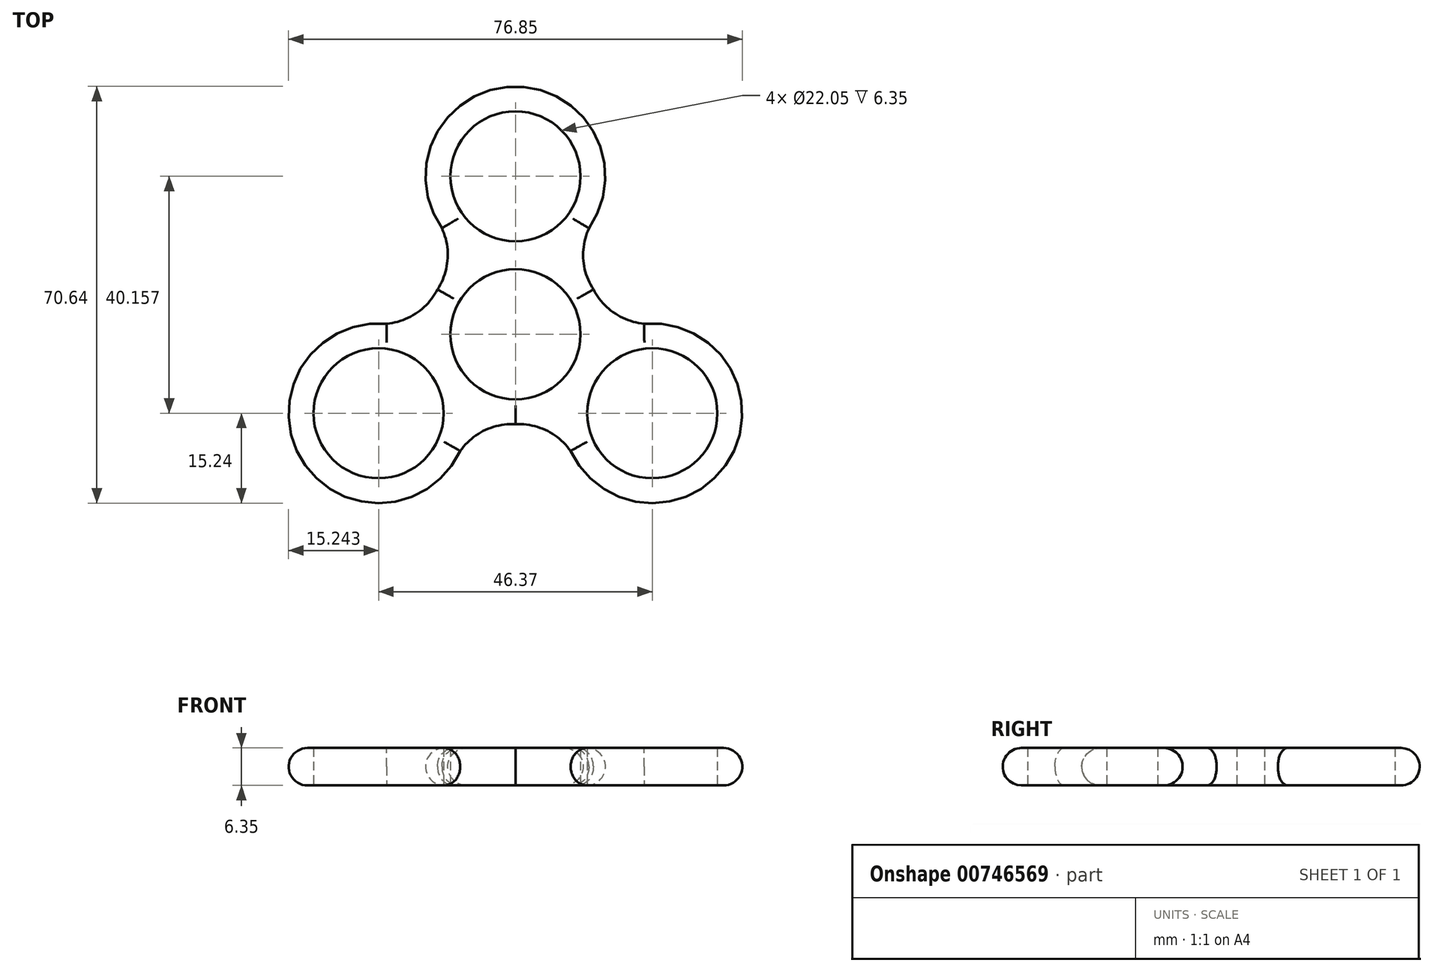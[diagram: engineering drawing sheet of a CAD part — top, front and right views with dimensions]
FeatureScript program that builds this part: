
annotation { "Feature Type Name" : "Feature", "Feature Type Description" : "" }
export const myFeature = defineFeature(function(context is Context, id is Id, definition is map)
    precondition{}
    {
        {
            var Q0;
            Q0=qCreatedBy(makeId("Top.planeOp"),FACE);
            var sketch = newSketch(context, id + "F0", { "sketchPlane" : qUnion([Q0])});
            skCircle(sketch, "E0", {"center": v(-0.7, 0.42) * mm, "radius": 11.02 * mm});
            skCircle(sketch, "E1", {"center": v(-0.7, 0.42) * mm, "radius": 15.24 * mm});
            skCircle(sketch, "E2", {"center": v(-0.7, 27.19) * mm, "radius": 11.02 * mm});
            skCircle(sketch, "E3", {"center": v(-0.7, 27.19) * mm, "radius": 15.24 * mm});
            skCircle(sketch, "E4.1.0", {"center": v(-23.88, -12.97) * mm, "radius": 15.24 * mm});
            skCircle(sketch, "E4.1.1", {"center": v(-23.88, -12.97) * mm, "radius": 11.02 * mm});
            skCircle(sketch, "E4.2.0", {"center": v(22.5, -12.97) * mm, "radius": 15.24 * mm});
            skCircle(sketch, "E4.2.1", {"center": v(22.5, -12.97) * mm, "radius": 11.02 * mm});
            skArc(sketch, "E5", {"start": v(-0.7, -14.82) * mm, "mid": v(-5.95, -15.9) * mm, "end": v(-10.04, -19.37) * mm});
            skArc(sketch, "E6.MirrorCS", {"start": v(-0.7, -14.82) * mm, "mid": v(4.57, -15.9) * mm, "end": v(8.66, -19.37) * mm});
            skArc(sketch, "E7.1.0", {"start": v(12.5, 8.04) * mm, "mid": v(10.8, 13.13) * mm, "end": v(11.76, 18.4) * mm});
            skArc(sketch, "E7.1.1", {"start": v(12.5, 8.04) * mm, "mid": v(16.06, 4.01) * mm, "end": v(21.12, 2.2) * mm});
            skArc(sketch, "E7.2.0", {"start": v(-13.9, 8.04) * mm, "mid": v(-17.44, 4.01) * mm, "end": v(-22.5, 2.2) * mm});
            skArc(sketch, "E7.2.1", {"start": v(-13.9, 8.04) * mm, "mid": v(-12.18, 13.13) * mm, "end": v(-13.15, 18.4) * mm});
            skLineSegment(sketch, "E7.anchor1", {"start": v(-0.7, 0.42) * mm, "end": v(-0.13, -25.57) * mm, "construction": true});
            skLineSegment(sketch, "E7.anchor2", {"start": v(-0.7, 0.42) * mm, "end": v(-23.48, 12.92) * mm, "construction": true});
            skSolve(sketch);
        }
        {
            var Q0;
            Q0=makeQuery(id+"F0.imprint","IMPRINT",FACE,{"disambiguationData":[TD([[makeQuery(id+"F0.imprint","IMPRINT",EDGE,{"derivedFrom":sQuery(id+"F0.wireOp",EDGE,"E2")}),-1.0]])]});
            var Q1;
            {var subQ0=sQuery(id+"F0.wireOp",EDGE,"E7.2.1");var subQ1=sQuery(id+"F0.wireOp",EDGE,"E1");var subQ2=makeQuery(id+"F0.imprint","INTERSECT",VERTEX,{"derivedFrom":[subQ1,subQ0]});Q1=makeQuery(id+"F0.imprint","IMPRINT",FACE,{"disambiguationData":[TD([[makeQuery(id+"F0.imprint","IMPRINT",EDGE,{"disambiguationData":[TD([[subQ2,1.0]])],"derivedFrom":subQ1}),-1.0]])]});}
            var Q2;
            {var subQ0=sQuery(id+"F0.wireOp",EDGE,"E7.2.0");var subQ1=sQuery(id+"F0.wireOp",EDGE,"E1");var subQ2=makeQuery(id+"F0.imprint","INTERSECT",VERTEX,{"derivedFrom":[subQ1,subQ0]});Q2=makeQuery(id+"F0.imprint","IMPRINT",FACE,{"disambiguationData":[TD([[makeQuery(id+"F0.imprint","IMPRINT",EDGE,{"disambiguationData":[TD([[subQ2,-1.0]])],"derivedFrom":subQ1}),-1.0]])]});}
            var Q3;
            {var subQ0=sQuery(id+"F0.wireOp",EDGE,"E7.1.0");var subQ1=sQuery(id+"F0.wireOp",EDGE,"E1");var subQ2=makeQuery(id+"F0.imprint","INTERSECT",VERTEX,{"derivedFrom":[subQ1,subQ0]});Q3=makeQuery(id+"F0.imprint","IMPRINT",FACE,{"disambiguationData":[TD([[makeQuery(id+"F0.imprint","IMPRINT",EDGE,{"disambiguationData":[TD([[subQ2,-1.0]])],"derivedFrom":subQ1}),-1.0]])]});}
            var Q4;
            {var subQ0=sQuery(id+"F0.wireOp",EDGE,"E7.1.1");var subQ1=sQuery(id+"F0.wireOp",EDGE,"E1");var subQ2=makeQuery(id+"F0.imprint","INTERSECT",VERTEX,{"derivedFrom":[subQ1,subQ0]});Q4=makeQuery(id+"F0.imprint","IMPRINT",FACE,{"disambiguationData":[TD([[makeQuery(id+"F0.imprint","IMPRINT",EDGE,{"disambiguationData":[TD([[subQ2,1.0]])],"derivedFrom":subQ1}),-1.0]])]});}
            var Q5;
            Q5=makeQuery(id+"F0.imprint","IMPRINT",FACE,{"disambiguationData":[TD([[makeQuery(id+"F0.imprint","IMPRINT",EDGE,{"derivedFrom":sQuery(id+"F0.wireOp",EDGE,"E0")}),-1.0]])]});
            var Q6;
            {var subQ0=sQuery(id+"F0.wireOp",EDGE,"E4.2.0");var subQ1=sQuery(id+"F0.wireOp",EDGE,"E1");var subQ2=makeQuery(id+"F0.imprint","INTERSECT",VERTEX,{"disambiguationData":[OD(0.0)],"derivedFrom":[subQ1,subQ0]});Q6=makeQuery(id+"F0.imprint","IMPRINT",FACE,{"disambiguationData":[TD([[makeQuery(id+"F0.imprint","IMPRINT",EDGE,{"disambiguationData":[TD([[subQ2,-1.0]])],"derivedFrom":subQ1}),1.0]])]});}
            var Q7;
            {var subQ0=sQuery(id+"F0.wireOp",EDGE,"E3");var subQ1=sQuery(id+"F0.wireOp",EDGE,"E1");var subQ2=makeQuery(id+"F0.imprint","INTERSECT",VERTEX,{"disambiguationData":[OD(0.0)],"derivedFrom":[subQ1,subQ0]});Q7=makeQuery(id+"F0.imprint","IMPRINT",FACE,{"disambiguationData":[TD([[makeQuery(id+"F0.imprint","IMPRINT",EDGE,{"disambiguationData":[TD([[subQ2,-1.0]])],"derivedFrom":subQ1}),1.0]])]});}
            var Q8;
            {var subQ0=sQuery(id+"F0.wireOp",EDGE,"E4.1.0");var subQ1=sQuery(id+"F0.wireOp",EDGE,"E1");var subQ2=makeQuery(id+"F0.imprint","INTERSECT",VERTEX,{"disambiguationData":[OD(0.0)],"derivedFrom":[subQ1,subQ0]});Q8=makeQuery(id+"F0.imprint","IMPRINT",FACE,{"disambiguationData":[TD([[makeQuery(id+"F0.imprint","IMPRINT",EDGE,{"disambiguationData":[TD([[subQ2,-1.0]])],"derivedFrom":subQ1}),1.0]])]});}
            var Q9;
            Q9=makeQuery(id+"F0.imprint","IMPRINT",FACE,{"disambiguationData":[TD([[makeQuery(id+"F0.imprint","IMPRINT",EDGE,{"derivedFrom":sQuery(id+"F0.wireOp",EDGE,"E4.1.1")}),-1.0]])]});
            var Q10;
            {var subQ0=sQuery(id+"F0.wireOp",EDGE,"E5");var subQ1=sQuery(id+"F0.wireOp",EDGE,"E1");var subQ2=makeQuery(id+"F0.imprint","INTERSECT",VERTEX,{"derivedFrom":[subQ1,subQ0]});Q10=makeQuery(id+"F0.imprint","IMPRINT",FACE,{"disambiguationData":[TD([[makeQuery(id+"F0.imprint","IMPRINT",EDGE,{"disambiguationData":[TD([[subQ2,1.0]])],"derivedFrom":subQ1}),-1.0]])]});}
            var Q11;
            {var subQ0=sQuery(id+"F0.wireOp",EDGE,"E6.MirrorCS");var subQ1=sQuery(id+"F0.wireOp",EDGE,"E1");var subQ2=makeQuery(id+"F0.imprint","INTERSECT",VERTEX,{"derivedFrom":[subQ1,subQ0]});Q11=makeQuery(id+"F0.imprint","IMPRINT",FACE,{"disambiguationData":[TD([[makeQuery(id+"F0.imprint","IMPRINT",EDGE,{"disambiguationData":[TD([[subQ2,-1.0]])],"derivedFrom":subQ1}),-1.0]])]});}
            var Q12;
            Q12=makeQuery(id+"F0.imprint","IMPRINT",FACE,{"disambiguationData":[TD([[makeQuery(id+"F0.imprint","IMPRINT",EDGE,{"derivedFrom":sQuery(id+"F0.wireOp",EDGE,"E4.2.1")}),-1.0]])]});
            extrude(context, id + "F1", {"entities" : qUnion([Q0, Q1, Q2, Q3, Q4, Q5, Q6, Q7, Q8, Q9, Q10, Q11, Q12]), "depth" : 6.35 * mm, "offsetDistance" : 25.4 * mm});
        }
        {
            var Q0;
            Q0=makeQuery(id+"F1.opExtrude","CAP_EDGE",EDGE,{"disambiguationData":[OSD([sQuery(id+"F0.wireOp",EDGE,"E3")])],"isStart":false});
            var Q1;
            Q1=makeQuery(id+"F1.opExtrude","CAP_EDGE",EDGE,{"disambiguationData":[OSD([sQuery(id+"F0.wireOp",EDGE,"E7.2.1")])],"isStart":false});
            var Q2;
            Q2=makeQuery(id+"F1.opExtrude","CAP_EDGE",EDGE,{"disambiguationData":[OSD([sQuery(id+"F0.wireOp",EDGE,"E7.2.0")])],"isStart":false});
            var Q3;
            Q3=makeQuery(id+"F1.opExtrude","CAP_EDGE",EDGE,{"disambiguationData":[OSD([sQuery(id+"F0.wireOp",EDGE,"E4.1.0")])],"isStart":false});
            var Q4;
            Q4=makeQuery(id+"F1.opExtrude","CAP_EDGE",EDGE,{"disambiguationData":[OSD([sQuery(id+"F0.wireOp",EDGE,"E5")])],"isStart":false});
            var Q5;
            Q5=makeQuery(id+"F1.opExtrude","CAP_EDGE",EDGE,{"disambiguationData":[OSD([sQuery(id+"F0.wireOp",EDGE,"E7.1.0")])],"isStart":false});
            var Q6;
            Q6=makeQuery(id+"F1.opExtrude","CAP_EDGE",EDGE,{"disambiguationData":[OSD([sQuery(id+"F0.wireOp",EDGE,"E4.2.0")])],"isStart":false});
            var Q7;
            Q7=makeQuery(id+"F1.opExtrude","CAP_EDGE",EDGE,{"disambiguationData":[OSD([sQuery(id+"F0.wireOp",EDGE,"E7.1.1")])],"isStart":false});
            var Q8;
            Q8=makeQuery(id+"F1.opExtrude","CAP_EDGE",EDGE,{"disambiguationData":[OSD([sQuery(id+"F0.wireOp",EDGE,"E6.MirrorCS")])],"isStart":false});
            fillet(context, id + "F2", {"entities" : qUnion([Q0, Q1, Q2, Q3, Q4, Q5, Q6, Q7, Q8]), "radius" : 3.17 * mm, "tangentPropagation" : true, "allowEdgeOverflow" : false});
        }
        {
            var Q0;
            Q0=makeQuery(id+"F1.opExtrude","CAP_EDGE",EDGE,{"disambiguationData":[OSD([sQuery(id+"F0.wireOp",EDGE,"E4.1.0")])],"isStart":true});
            var Q1;
            Q1=makeQuery(id+"F1.opExtrude","CAP_EDGE",EDGE,{"disambiguationData":[OSD([sQuery(id+"F0.wireOp",EDGE,"E5")])],"isStart":true});
            var Q2;
            Q2=makeQuery(id+"F1.opExtrude","CAP_EDGE",EDGE,{"disambiguationData":[OSD([sQuery(id+"F0.wireOp",EDGE,"E4.2.0")])],"isStart":true});
            var Q3;
            Q3=makeQuery(id+"F1.opExtrude","CAP_EDGE",EDGE,{"disambiguationData":[OSD([sQuery(id+"F0.wireOp",EDGE,"E7.1.1")])],"isStart":true});
            var Q4;
            Q4=makeQuery(id+"F1.opExtrude","CAP_EDGE",EDGE,{"disambiguationData":[OSD([sQuery(id+"F0.wireOp",EDGE,"E6.MirrorCS")])],"isStart":true});
            var Q5;
            Q5=makeQuery(id+"F1.opExtrude","CAP_EDGE",EDGE,{"disambiguationData":[OSD([sQuery(id+"F0.wireOp",EDGE,"E7.1.0")])],"isStart":true});
            var Q6;
            Q6=makeQuery(id+"F1.opExtrude","CAP_EDGE",EDGE,{"disambiguationData":[OSD([sQuery(id+"F0.wireOp",EDGE,"E7.2.1")])],"isStart":true});
            var Q7;
            Q7=makeQuery(id+"F1.opExtrude","CAP_EDGE",EDGE,{"disambiguationData":[OSD([sQuery(id+"F0.wireOp",EDGE,"E7.2.0")])],"isStart":true});
            var Q8;
            Q8=makeQuery(id+"F1.opExtrude","CAP_EDGE",EDGE,{"disambiguationData":[OSD([sQuery(id+"F0.wireOp",EDGE,"E3")])],"isStart":true});
            fillet(context, id + "F3", {"entities" : qUnion([Q0, Q1, Q2, Q3, Q4, Q5, Q6, Q7, Q8]), "radius" : 3.17 * mm, "tangentPropagation" : true, "allowEdgeOverflow" : false});
        }
    });
